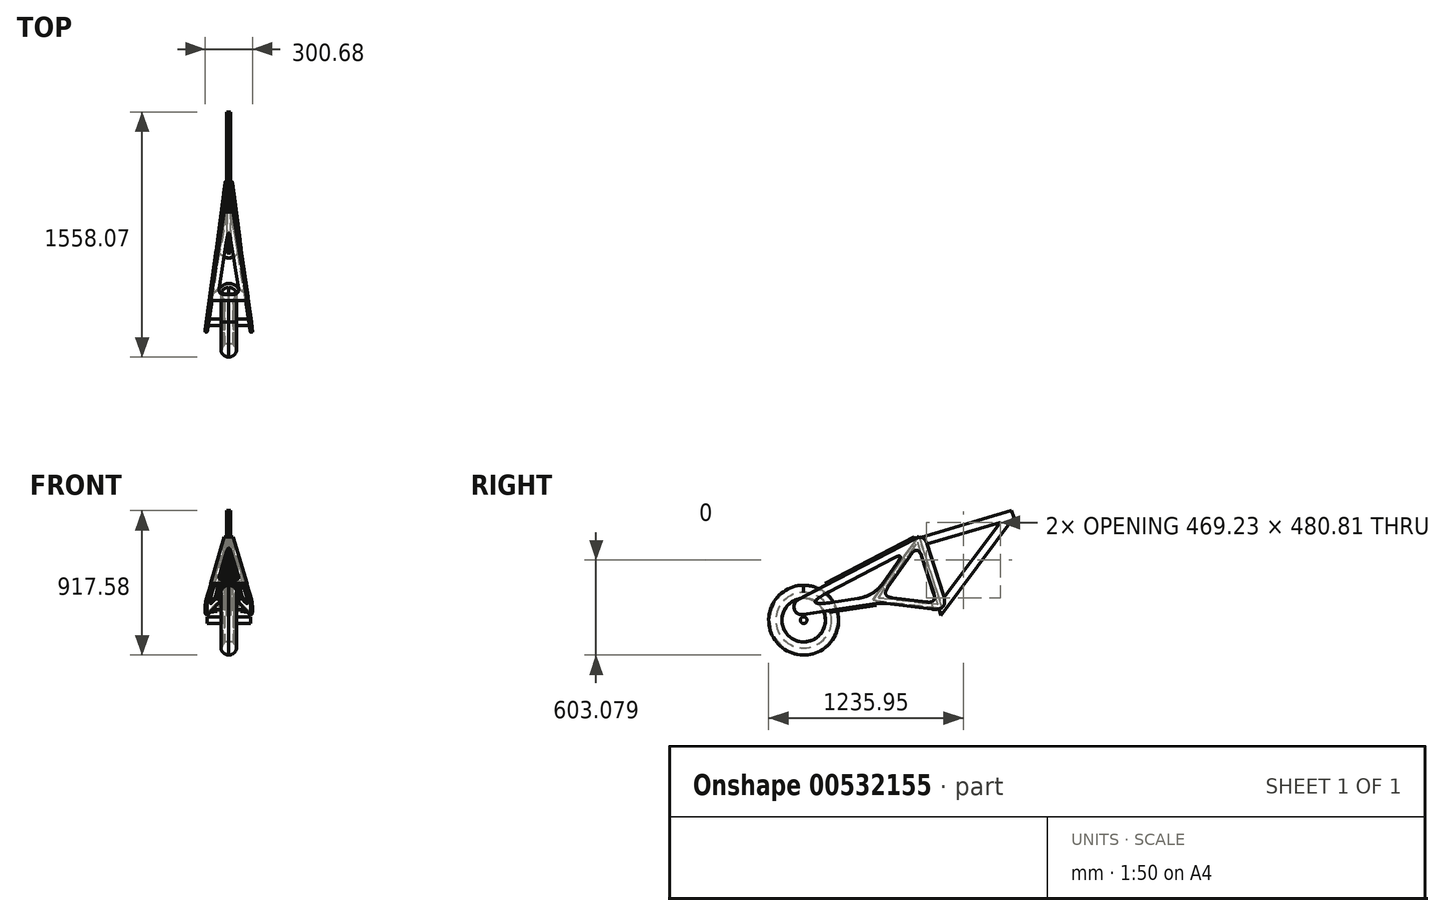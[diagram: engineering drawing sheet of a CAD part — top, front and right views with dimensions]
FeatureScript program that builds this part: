
annotation { "Feature Type Name" : "Feature", "Feature Type Description" : "" }
export const myFeature = defineFeature(function(context is Context, id is Id, definition is map)
    precondition{}
    {
        {
            var Q0;
            Q0=qCreatedBy(makeId("Right.planeOp"),FACE);
            var sketch = newSketch(context, id + "F0", { "sketchPlane" : qUnion([Q0])});
            skLineSegment(sketch, "E0", {"start": v(-1122.6, -29.4) * mm, "end": v(-831.27, 379.28) * mm});
            skLineSegment(sketch, "E1", {"start": v(-831.27, 379.28) * mm, "end": v(-682.15, -80.49) * mm});
            skLineSegment(sketch, "E2", {"start": v(-682.15, -80.49) * mm, "end": v(-235.77, 518.94) * mm});
            skLineSegment(sketch, "E3", {"start": v(-820.77, 346.9) * mm, "end": v(-235.77, 518.94) * mm});
            skLineSegment(sketch, "E4", {"start": v(-1122.6, -29.4) * mm, "end": v(-682.15, -80.49) * mm});
            skLineSegment(sketch, "E5", {"start": v(-291.82, 608.35) * mm, "end": v(115.38, -439.2) * mm});
            skLineSegment(sketch, "E6", {"start": v(-14.33, -30.36) * mm, "end": v(-39.71, -40.22) * mm});
            skLineSegment(sketch, "E7", {"start": v(-14.33, -30.36) * mm, "end": v(-14.33, -432.63) * mm});
            skLineSegment(sketch, "E8", {"start": v(-14.33, -30.36) * mm, "end": v(149.04, -450.65) * mm});
            skSolve(sketch);
        }
        {
            var Q0;
            Q0=qCreatedBy(makeId("Right.planeOp"),FACE);
            var sketch = newSketch(context, id + "F1", { "sketchPlane" : qUnion([Q0])});
            skCircle(sketch, "E9", {"center": v(-1562.05, -156.67) * mm, "radius": 222 * mm});
            skLineSegment(sketch, "E10", {"start": v(660.86, -378.67) * mm, "end": v(-1840.95, -378.67) * mm, "construction": true});
            skSolve(sketch);
        }
        {
            var Q0;
            Q0=qCreatedBy(makeId("Front.planeOp"),FACE);
            var sketch = newSketch(context, id + "F2", { "sketchPlane" : qUnion([Q0])});
            skLineSegment(sketch, "E11.0", {"start": v(0, 65.33) * mm, "end": v(0, -378.67) * mm, "construction": true});
            skFitSpline(sketch, "E12", {"points": [v(0, 65.33) * mm, v(-50, 19.93) * mm], "startDerivative": vector(-52.78, 0) * mm, "endDerivative": vector(0, -87.78) * mm});
            skFitSpline(sketch, "E13", {"points": [v(-50, 19.93) * mm, v(-31.08, -18.17) * mm], "startDerivative": vector(0, -29.8) * mm, "endDerivative": vector(32.97, -29.47) * mm});
            skFitSpline(sketch, "E14.0", {"points": [v(-44.5, 19.93) * mm, v(-44.5, 19.5) * mm, v(-44.46, 18.5) * mm, v(-44.16, 16.18) * mm, v(-43.4, 12.74) * mm, v(-41.86, 8.1) * mm, v(-39.08, 1.57) * mm, v(-35.33, -4.96) * mm, v(-30.93, -10.62) * mm, v(-28.6, -13.01) * mm, v(-27.42, -14.07) * mm]});
            skFitSpline(sketch, "E14.1", {"points": [v(0, 59.83) * mm, v(-0.89, 59.83) * mm, v(-2.83, 59.73) * mm, v(-7.2, 59.08) * mm, v(-13.33, 57.4) * mm, v(-21.02, 54.03) * mm, v(-28.45, 49.4) * mm, v(-35.02, 43.58) * mm, v(-40.22, 36.74) * mm, v(-43.64, 28.95) * mm, v(-44.5, 23.08) * mm, v(-44.5, 19.93) * mm]});
            skLineSegment(sketch, "E15", {"start": v(0, 65.33) * mm, "end": v(0, 59.83) * mm});
            skLineSegment(sketch, "E16", {"start": v(-31.08, -18.17) * mm, "end": v(-27.42, -14.07) * mm});
            skPoint(sketch, "E17", {"position": v(0, -156.67) * mm});
            skSolve(sketch);
        }
        {
            var Q0;
            Q0=qCreatedBy(makeId("Right.planeOp"),FACE);
            var sketch = newSketch(context, id + "F3", { "sketchPlane" : qUnion([Q0])});
            skLineSegment(sketch, "E18.0", {"start": v(0, 65.33) * mm, "end": v(0, -378.67) * mm, "construction": true});
            skPoint(sketch, "E18.1", {"position": v(0, -156.67) * mm});
            skCircle(sketch, "E19", {"center": v(0, -156.67) * mm, "radius": 222 * mm});
            skSolve(sketch);
        }
        {
            var Q0;
            Q0 = qSketchRegion(id + "F2", true);
            var Q1;
            Q1=sQuery(id+"F3.wireOp",EDGE,"E19");
            revolve(context, id + "F4", {"entities" : qUnion([Q0]), "axis" : qUnion([Q1]), "revolveType" : RevolveType.FULL});
        }
        {
            var Q0;
            Q0=makeQuery(id+"F4.opRevolve","SWEPT_BODY",BODY,{"disambiguationData":[OSD([sQuery(id+"F2.wireOp",EDGE,"E12"),sQuery(id+"F2.wireOp",EDGE,"E13"),sQuery(id+"F2.wireOp",EDGE,"E14.0"),sQuery(id+"F2.wireOp",EDGE,"E14.1"),sQuery(id+"F2.wireOp",EDGE,"E15"),sQuery(id+"F2.wireOp",EDGE,"E16")])]});
            var Q1;
            Q1=qCreatedBy(makeId("Right.planeOp"),FACE);
            mirror(context, id + "F5", {"operationType" : NewBodyOperationType.ADD, "entities" : qUnion([Q0]), "mirrorPlane" : qUnion([Q1])});
        }
        {
            var Q0;
            Q0=sQuery(id+"F2.wireOp",EDGE,"E11.0");
            cPoint(context, id + "F6", {"entities" : qUnion([Q0]), "parameter" : 0.5});
        }
        {
            var Q0;
            Q0=makeQuery(id+"F4.opRevolve","SWEPT_BODY",BODY,{"disambiguationData":[OSD([sQuery(id+"F2.wireOp",EDGE,"E12"),sQuery(id+"F2.wireOp",EDGE,"E13"),sQuery(id+"F2.wireOp",EDGE,"E14.0"),sQuery(id+"F2.wireOp",EDGE,"E14.1"),sQuery(id+"F2.wireOp",EDGE,"E15"),sQuery(id+"F2.wireOp",EDGE,"E16")])]});
            var Q1;
            Q1 = qCreatedBy(id + "F6" ,VERTEX);
            var Q2;
            Q2=sQuery(id+"F1.wireOp",VERTEX,"E9.center");
            transform(context, id + "F7", {"entities" : qUnion([Q0]), "transformType" : TransformType.TRANSLATION_ENTITY, "oppositeDirectionEntity" : false, "transformLine" : qUnion([Q1, Q2]), "makeCopy" : false});
        }
        {
            var Q0;
            Q0=qCreatedBy(makeId("Right.planeOp"),FACE);
            var sketch = newSketch(context, id + "F8", { "sketchPlane" : qUnion([Q0])});
            skCircle(sketch, "E20.0.0", {"center": v(-1562.05, -156.67) * mm, "radius": 222 * mm, "construction": true});
            skCircle(sketch, "E21", {"center": v(-1562.05, -156.67) * mm, "radius": 21.1 * mm});
            skSolve(sketch);
        }
        {
            var Q0;
            Q0 = qSketchRegion(id + "F8", true);
            extrude(context, id + "F9", {"entities" : qUnion([Q0]), "endBound" : BoundingType.SYMMETRIC, "depth" : 275 * mm, "offsetDistance" : 25 * mm});
        }
        {
            var Q0;
            Q0=qCreatedBy(makeId("Right.planeOp"),FACE);
            var sketch = newSketch(context, id + "F10", { "sketchPlane" : qUnion([Q0])});
            skCircle(sketch, "E22.0.0", {"center": v(-1562.05, -156.67) * mm, "radius": 222 * mm, "construction": true});
            skCircle(sketch, "E23", {"center": v(-1562.05, -156.67) * mm, "radius": 137.5 * mm});
            skSolve(sketch);
        }
        {
            var Q0;
            Q0 = qSketchRegion(id + "F10", true);
            extrude(context, id + "F11", {"entities" : qUnion([Q0]), "operationType" : NewBodyOperationType.ADD, "endBound" : BoundingType.SYMMETRIC, "depth" : 70 * mm, "offsetDistance" : 25 * mm});
        }
        {
            var Q0;
            {var subQ0=sQuery(id+"F0.wireOp",EDGE,"E0");Q0=makeQuery(id+"F0.imprint","IMPRINT",FACE,{"disambiguationData":[TD([[makeQuery(id+"F0.imprint","IMPRINT",EDGE,{"derivedFrom":subQ0}),-1.0]])]});}
            extrude(context, id + "F12", {"entities" : qUnion([Q0]), "depth" : (135 / 2) * mm, "offsetDistance" : 25 * mm});
        }
        {
            var Q0;
            Q0=makeQuery(id+"F12.opExtrude","CAP_EDGE",EDGE,{"disambiguationData":[OSD([sQuery(id+"F0.wireOp",EDGE,"E1")])],"isStart":false});
            chamfer(context, id + "F13", {"entities" : qUnion([Q0]), "chamferType" : ChamferType.OFFSET_ANGLE, "width" : 55 * mm, "oppositeDirection" : false, "angle" : 82 * degree, "tangentPropagation" : true});
        }
        {
            var Q0;
            Q0=makeQuery(id+"F12.opExtrude","SWEPT_BODY",BODY,{"disambiguationData":[OSD([sQuery(id+"F0.wireOp",EDGE,"E0"),sQuery(id+"F0.wireOp",EDGE,"E1"),sQuery(id+"F0.wireOp",EDGE,"E4")])]});
            var Q1;
            Q1=qCreatedBy(makeId("Right.planeOp"),FACE);
            mirror(context, id + "F14", {"operationType" : NewBodyOperationType.ADD, "entities" : qUnion([Q0]), "mirrorPlane" : qUnion([Q1])});
        }
        {
            var Q0;
            {var subQ0=makeQuery(id+"F12.opExtrude","SWEPT_FACE",FACE,{"disambiguationData":[OSD([sQuery(id+"F0.wireOp",EDGE,"E0")])]});Q0=makeQuery(id+"F14.boolean.opBoolean","MERGE",FACE,{"derivedFrom":[subQ0,makeQuery(id+"F14.opPattern","COPY",FACE,{"derivedFrom":subQ0,"instanceName":"1"})]});}
            var Q1;
            {var subQ0=makeQuery(id+"F12.opExtrude","SWEPT_FACE",FACE,{"disambiguationData":[OSD([sQuery(id+"F0.wireOp",EDGE,"E4")])]});Q1=makeQuery(id+"F14.boolean.opBoolean","MERGE",FACE,{"derivedFrom":[subQ0,makeQuery(id+"F14.opPattern","COPY",FACE,{"derivedFrom":subQ0,"instanceName":"1"})]});}
            shell(context, id + "F15", {"entities" : qUnion([Q0, Q1]), "thickness" : 10 * mm});
        }
        {
            var Q0;
            Q0=qCreatedBy(makeId("Right.planeOp"),FACE);
            var sketch = newSketch(context, id + "F16", { "sketchPlane" : qUnion([Q0])});
            skLineSegment(sketch, "E24.0.0", {"start": v(-1114.03, -17.39) * mm, "end": v(-831.27, 379.28) * mm, "construction": true});
            skLineSegment(sketch, "E24.0.1", {"start": v(-1114.03, -17.39) * mm, "end": v(-1109.65, -30.9) * mm, "construction": true});
            skLineSegment(sketch, "E24.0.2", {"start": v(-682.15, -80.49) * mm, "end": v(-1109.65, -30.9) * mm, "construction": true});
            skLineSegment(sketch, "E24.0.3", {"start": v(-682.15, -80.49) * mm, "end": v(-831.27, 379.28) * mm, "construction": true});
            skLineSegment(sketch, "E25.0", {"start": v(-709.35, -58.2) * mm, "end": v(-837.7, 337.53) * mm});
            skLineSegment(sketch, "E25.1", {"start": v(-709.35, -58.2) * mm, "end": v(-1088.45, -14.23) * mm});
            skLineSegment(sketch, "E25.2", {"start": v(-1088.45, -14.23) * mm, "end": v(-837.7, 337.53) * mm});
            skSolve(sketch);
        }
        {
            var Q0;
            Q0 = qSketchRegion(id + "F16", true);
            var Q1;
            Q1 = qConstructionFilter(qBodyType(qCreatedBy(id + "F16" ,EDGE), BodyType.WIRE), ConstructionObject.NO);
            extrude(context, id + "F17", {"entities" : qUnion([Q0]), "operationType" : NewBodyOperationType.REMOVE, "surfaceEntities" : qUnion([Q1]), "endBound" : BoundingType.SYMMETRIC, "depth" : 174 * mm, "offsetDistance" : 25 * mm});
        }
        {
            var Q0;
            Q0=qCreatedBy(makeId("Right.planeOp"),FACE);
            var sketch = newSketch(context, id + "F18", { "sketchPlane" : qUnion([Q0])});
            skLineSegment(sketch, "E26.0.0", {"start": v(-820.77, 346.9) * mm, "end": v(-682.15, -80.49) * mm, "construction": true});
            skLineSegment(sketch, "E26.0.1", {"start": v(-682.15, -80.49) * mm, "end": v(-249.76, 500.15) * mm, "construction": true});
            skLineSegment(sketch, "E26.0.2", {"start": v(-249.76, 500.15) * mm, "end": v(-254.88, 513.32) * mm, "construction": true});
            skLineSegment(sketch, "E26.0.3", {"start": v(-254.88, 513.32) * mm, "end": v(-820.77, 346.9) * mm, "construction": true});
            skLineSegment(sketch, "E27.0", {"start": v(-242.3, 538.9) * mm, "end": v(-847.4, 360.96) * mm});
            skLineSegment(sketch, "E27.1", {"start": v(-225.98, 496.93) * mm, "end": v(-242.3, 538.9) * mm});
            skLineSegment(sketch, "E27.2", {"start": v(-689.59, -125.63) * mm, "end": v(-225.98, 496.93) * mm});
            skLineSegment(sketch, "E27.3", {"start": v(-847.4, 360.96) * mm, "end": v(-689.59, -125.63) * mm});
            skLineSegment(sketch, "E28.0", {"start": v(-782.71, 326.82) * mm, "end": v(-671.53, -16) * mm});
            skLineSegment(sketch, "E28.1", {"start": v(-313.48, 464.81) * mm, "end": v(-782.71, 326.82) * mm});
            skLineSegment(sketch, "E28.2", {"start": v(-671.53, -16) * mm, "end": v(-313.48, 464.81) * mm});
            skSolve(sketch);
        }
        {
            var Q0;
            Q0 = qSketchRegion(id + "F18", true);
            var Q1;
            {var subQ0=sQuery(id+"F0.wireOp",EDGE,"E1");Q1=makeQuery(id+"F13.opChamfer","BLEND_VERTEX",VERTEX,{"blendedFrom":[makeQuery(id+"F12.opExtrude","CAP_EDGE",EDGE,{"disambiguationData":[OSD([subQ0])],"isStart":false}),makeQuery(id+"F12.opExtrude","SWEPT_FACE",FACE,{"disambiguationData":[OSD([sQuery(id+"F0.wireOp",EDGE,"E0")])]}),makeQuery(id+"F12.opExtrude","SWEPT_FACE",FACE,{"disambiguationData":[OSD([subQ0])]})],"blendedInto":[makeQuery(id+"F12.opExtrude","SWEPT_FACE",FACE,{"disambiguationData":[OSD([sQuery(id+"F0.wireOp",EDGE,"E0")])]}),makeQuery(id+"F12.opExtrude","SWEPT_FACE",FACE,{"disambiguationData":[OSD([subQ0])]})]});}
            extrude(context, id + "F19", {"entities" : qUnion([Q0]), "operationType" : NewBodyOperationType.ADD, "endBound" : BoundingType.UP_TO_VERTEX, "depth" : 25 * mm, "endBoundEntityVertex" : qUnion([Q1]), "offsetDistance" : 25 * mm});
        }
        {
            var Q0;
            Q0=makeQuery(id+"F12.opExtrude","SWEPT_BODY",BODY,{"disambiguationData":[OSD([sQuery(id+"F0.wireOp",EDGE,"E0"),sQuery(id+"F0.wireOp",EDGE,"E1"),sQuery(id+"F0.wireOp",EDGE,"E4")])]});
            var Q1;
            Q1=qCreatedBy(makeId("Right.planeOp"),FACE);
            mirror(context, id + "F20", {"operationType" : NewBodyOperationType.ADD, "entities" : qUnion([Q0]), "mirrorPlane" : qUnion([Q1])});
        }
        {
            var Q0;
            Q0=makeQuery(id+"F13.opChamfer","BLEND_FACE",FACE,{"disambiguationData":[OSD([sQuery(id+"F0.wireOp",EDGE,"E1")])]});
            var sketch = newSketch(context, id + "F21", { "sketchPlane" : qUnion([Q0])});
            skLineSegment(sketch, "E29.0", {"start": v(-711.61, -51.04) * mm, "end": v(-834.34, 323.68) * mm});
            skLineSegment(sketch, "E29.1", {"start": v(-1068, -9.4) * mm, "end": v(-711.61, -51.04) * mm});
            skLineSegment(sketch, "E29.2", {"start": v(-834.34, 323.68) * mm, "end": v(-1068, -9.4) * mm});
            skLineSegment(sketch, "E30.0", {"start": v(-634.82, -108.8) * mm, "end": v(-797.78, 388.75) * mm});
            skLineSegment(sketch, "E31.0", {"start": v(-919.6, 271.8) * mm, "end": v(-1115.15, -6.97) * mm});
            skLineSegment(sketch, "E32", {"start": v(-1634.51, -50.02) * mm, "end": v(-797.78, 388.75) * mm});
            skLineSegment(sketch, "E33.0", {"start": v(-1590.61, -80.07) * mm, "end": v(-919.6, 271.8) * mm});
            skLineSegment(sketch, "E34.0", {"start": v(-1069.42, -49.51) * mm, "end": v(-637.72, -99.95) * mm});
            skLineSegment(sketch, "E35", {"start": v(-1069.42, -49.51) * mm, "end": v(-1618.77, -133.97) * mm});
            skLineSegment(sketch, "E36", {"start": v(-1618.77, -133.97) * mm, "end": v(-1634.51, -50.02) * mm});
            skLineSegment(sketch, "E37.0", {"start": v(-1115.15, -6.97) * mm, "end": v(-1590.61, -80.07) * mm});
            skSolve(sketch);
        }
        {
            var Q0;
            Q0 = qSketchRegion(id + "F21", true);
            extrude(context, id + "F22", {"entities" : qUnion([Q0]), "depth" : 12 * mm, "offsetDistance" : 25 * mm});
        }
        {
            var Q0;
            Q0=makeQuery(id+"F22.opExtrude","SWEPT_EDGE",EDGE,{"disambiguationData":[OSD([sQuery(id+"F21.wireOp",EDGE,"E33.0"),sQuery(id+"F21.wireOp",EDGE,"E37.0")])]});
            fillet(context, id + "F23", {"entities" : qUnion([Q0]), "radius" : 34.8 * mm, "tangentPropagation" : true, "rho" : 0.5, "crossSection" : FilletCrossSection.CONIC, "allowEdgeOverflow" : false});
        }
        {
            var Q0;
            Q0=makeQuery(id+"F22.opExtrude","SWEPT_EDGE",EDGE,{"disambiguationData":[OSD([sQuery(id+"F21.wireOp",EDGE,"E31.0"),sQuery(id+"F21.wireOp",EDGE,"E33.0")])]});
            fillet(context, id + "F24", {"entities" : qUnion([Q0]), "radius" : 18.98 * mm, "tangentPropagation" : true, "rho" : 0.5, "crossSection" : FilletCrossSection.CONIC, "allowEdgeOverflow" : false});
        }
        {
            var Q0;
            Q0=makeQuery(id+"F22.opExtrude","SWEPT_EDGE",EDGE,{"disambiguationData":[OSD([sQuery(id+"F21.wireOp",EDGE,"E31.0"),sQuery(id+"F21.wireOp",EDGE,"E37.0")])]});
            var Q1;
            Q1=makeQuery(id+"F22.opExtrude","SWEPT_EDGE",EDGE,{"disambiguationData":[OSD([sQuery(id+"F21.wireOp",EDGE,"E34.0"),sQuery(id+"F21.wireOp",EDGE,"E35")])]});
            fillet(context, id + "F25", {"entities" : qUnion([Q0, Q1]), "radius" : 253.46 * mm, "tangentPropagation" : true, "rho" : 0.5, "crossSection" : FilletCrossSection.CONIC, "allowEdgeOverflow" : false});
        }
        {
            var Q0;
            Q0=makeQuery(id+"F22.opExtrude","SWEPT_EDGE",EDGE,{"disambiguationData":[OSD([sQuery(id+"F21.wireOp",EDGE,"E29.1"),sQuery(id+"F21.wireOp",EDGE,"E29.2")])]});
            var Q1;
            Q1=makeQuery(id+"F22.opExtrude","SWEPT_EDGE",EDGE,{"disambiguationData":[OSD([sQuery(id+"F21.wireOp",EDGE,"E29.0"),sQuery(id+"F21.wireOp",EDGE,"E29.2")])]});
            var Q2;
            Q2=makeQuery(id+"F22.opExtrude","SWEPT_EDGE",EDGE,{"disambiguationData":[OSD([sQuery(id+"F21.wireOp",EDGE,"E29.0"),sQuery(id+"F21.wireOp",EDGE,"E29.1")])]});
            fillet(context, id + "F26", {"entities" : qUnion([Q0, Q1, Q2]), "radius" : 43.22 * mm, "tangentPropagation" : true, "rho" : 0.5, "crossSection" : FilletCrossSection.CONIC, "allowEdgeOverflow" : false});
        }
        {
            var Q0;
            Q0=makeQuery(id+"F22.opExtrude","SWEPT_EDGE",EDGE,{"disambiguationData":[OSD([sQuery(id+"F21.wireOp",EDGE,"E30.0"),sQuery(id+"F21.wireOp",EDGE,"E34.0")])]});
            fillet(context, id + "F27", {"entities" : qUnion([Q0]), "radius" : 70.1 * mm, "tangentPropagation" : true, "rho" : 0.5, "crossSection" : FilletCrossSection.CONIC, "allowEdgeOverflow" : false});
        }
        {
            var Q0;
            Q0=makeQuery(id+"F22.opExtrude","SWEPT_EDGE",EDGE,{"disambiguationData":[OSD([sQuery(id+"F21.wireOp",EDGE,"E30.0"),sQuery(id+"F21.wireOp",EDGE,"E32")])]});
            fillet(context, id + "F28", {"entities" : qUnion([Q0]), "radius" : 54.23 * mm, "tangentPropagation" : true, "rho" : 0.5, "crossSection" : FilletCrossSection.CONIC, "allowEdgeOverflow" : false});
        }
        {
            var Q0;
            Q0=makeQuery(id+"F22.opExtrude","SWEPT_EDGE",EDGE,{"disambiguationData":[OSD([sQuery(id+"F21.wireOp",EDGE,"E35"),sQuery(id+"F21.wireOp",EDGE,"E36")])]});
            var Q1;
            Q1=makeQuery(id+"F22.opExtrude","SWEPT_EDGE",EDGE,{"disambiguationData":[OSD([sQuery(id+"F21.wireOp",EDGE,"E32"),sQuery(id+"F21.wireOp",EDGE,"E36")])]});
            fillet(context, id + "F29", {"entities" : qUnion([Q0, Q1]), "radius" : 55.18 * mm, "tangentPropagation" : true, "rho" : 0.5, "crossSection" : FilletCrossSection.CONIC, "allowEdgeOverflow" : false});
        }
        {
            var Q0;
            Q0=makeQuery(id+"F22.opExtrude","SWEPT_BODY",BODY,{"disambiguationData":[OSD([sQuery(id+"F21.wireOp",EDGE,"E29.0"),sQuery(id+"F21.wireOp",EDGE,"E29.1"),sQuery(id+"F21.wireOp",EDGE,"E29.2"),sQuery(id+"F21.wireOp",EDGE,"6da51f72-84aa-4f4f-bf31-fd4d25252199.0"),sQuery(id+"F21.wireOp",EDGE,"E30.0"),sQuery(id+"F21.wireOp",EDGE,"E31.0"),sQuery(id+"F21.wireOp",EDGE,"LE8Z4zwS-jpNQ-33Xu-anEL-P9uhT3QDLyb7"),sQuery(id+"F21.wireOp",EDGE,"292b67fa-2026-495d-969f-669d1d39df75.0"),sQuery(id+"F21.wireOp",EDGE,"51c220b2-5f74-4f39-8bed-7295a8b32c18.trimOffspring"),sQuery(id+"F21.wireOp",EDGE,"45e865d4-9d95-4cce-95a6-58d17cf9b12f.0")])]});
            var Q1;
            Q1=qCreatedBy(makeId("Right.planeOp"),FACE);
            mirror(context, id + "F30", {"entities" : qUnion([Q0]), "mirrorPlane" : qUnion([Q1])});
        }
        {
            var Q0;
            {var subQ0=sQuery(id+"F21.wireOp",EDGE,"E36");var subQ1=sQuery(id+"F21.wireOp",EDGE,"E32");Q0=makeQuery(id+"F30.opPattern","COPY",VERTEX,{"derivedFrom":makeQuery(id+"F29.opFillet","BLEND_VERTEX",VERTEX,{"blendedFrom":[makeQuery(id+"F22.opExtrude","SWEPT_EDGE",EDGE,{"disambiguationData":[OSD([subQ1,subQ0])]}),makeQuery(id+"F22.opExtrude","SWEPT_FACE",FACE,{"disambiguationData":[OSD([subQ1])]}),makeQuery(id+"F22.opExtrude","CAP_FACE",FACE,{"disambiguationData":[OSD([sQuery(id+"F21.wireOp",EDGE,"E29.0"),sQuery(id+"F21.wireOp",EDGE,"E29.1"),sQuery(id+"F21.wireOp",EDGE,"E29.2"),sQuery(id+"F21.wireOp",EDGE,"E30.0"),sQuery(id+"F21.wireOp",EDGE,"E31.0"),subQ1,sQuery(id+"F21.wireOp",EDGE,"E33.0"),sQuery(id+"F21.wireOp",EDGE,"E34.0"),sQuery(id+"F21.wireOp",EDGE,"E35"),subQ0,sQuery(id+"F21.wireOp",EDGE,"E37.0")])],"isStart":true})],"blendedInto":[makeQuery(id+"F22.opExtrude","SWEPT_FACE",FACE,{"disambiguationData":[OSD([subQ1])]}),makeQuery(id+"F22.opExtrude","CAP_FACE",FACE,{"disambiguationData":[OSD([sQuery(id+"F21.wireOp",EDGE,"E29.0"),sQuery(id+"F21.wireOp",EDGE,"E29.1"),sQuery(id+"F21.wireOp",EDGE,"E29.2"),sQuery(id+"F21.wireOp",EDGE,"E30.0"),sQuery(id+"F21.wireOp",EDGE,"E31.0"),subQ1,sQuery(id+"F21.wireOp",EDGE,"E33.0"),sQuery(id+"F21.wireOp",EDGE,"E34.0"),sQuery(id+"F21.wireOp",EDGE,"E35"),subQ0,sQuery(id+"F21.wireOp",EDGE,"E37.0")])],"isStart":true})]}),"instanceName":"1"});}
            var Q1;
            {var subQ0=sQuery(id+"F21.wireOp",EDGE,"E36");var subQ1=sQuery(id+"F21.wireOp",EDGE,"E32");Q1=makeQuery(id+"F29.opFillet","BLEND_VERTEX",VERTEX,{"blendedFrom":[makeQuery(id+"F22.opExtrude","SWEPT_EDGE",EDGE,{"disambiguationData":[OSD([subQ1,subQ0])]}),makeQuery(id+"F22.opExtrude","SWEPT_FACE",FACE,{"disambiguationData":[OSD([subQ1])]}),makeQuery(id+"F22.opExtrude","CAP_FACE",FACE,{"disambiguationData":[OSD([sQuery(id+"F21.wireOp",EDGE,"E29.0"),sQuery(id+"F21.wireOp",EDGE,"E29.1"),sQuery(id+"F21.wireOp",EDGE,"E29.2"),sQuery(id+"F21.wireOp",EDGE,"E30.0"),sQuery(id+"F21.wireOp",EDGE,"E31.0"),subQ1,sQuery(id+"F21.wireOp",EDGE,"E33.0"),sQuery(id+"F21.wireOp",EDGE,"E34.0"),sQuery(id+"F21.wireOp",EDGE,"E35"),subQ0,sQuery(id+"F21.wireOp",EDGE,"E37.0")])],"isStart":true})],"blendedInto":[makeQuery(id+"F22.opExtrude","SWEPT_FACE",FACE,{"disambiguationData":[OSD([subQ1])]}),makeQuery(id+"F22.opExtrude","CAP_FACE",FACE,{"disambiguationData":[OSD([sQuery(id+"F21.wireOp",EDGE,"E29.0"),sQuery(id+"F21.wireOp",EDGE,"E29.1"),sQuery(id+"F21.wireOp",EDGE,"E29.2"),sQuery(id+"F21.wireOp",EDGE,"E30.0"),sQuery(id+"F21.wireOp",EDGE,"E31.0"),subQ1,sQuery(id+"F21.wireOp",EDGE,"E33.0"),sQuery(id+"F21.wireOp",EDGE,"E34.0"),sQuery(id+"F21.wireOp",EDGE,"E35"),subQ0,sQuery(id+"F21.wireOp",EDGE,"E37.0")])],"isStart":true})]});}
            var Q2;
            {var subQ0=sQuery(id+"F21.wireOp",EDGE,"E32");var subQ1=sQuery(id+"F21.wireOp",EDGE,"E30.0");Q2=makeQuery(id+"F30.opPattern","COPY",VERTEX,{"derivedFrom":makeQuery(id+"F28.opFillet","BLEND_VERTEX",VERTEX,{"blendedFrom":[makeQuery(id+"F22.opExtrude","SWEPT_EDGE",EDGE,{"disambiguationData":[OSD([subQ1,subQ0])]}),makeQuery(id+"F22.opExtrude","SWEPT_FACE",FACE,{"disambiguationData":[OSD([subQ0])]}),makeQuery(id+"F22.opExtrude","CAP_FACE",FACE,{"disambiguationData":[OSD([sQuery(id+"F21.wireOp",EDGE,"E29.0"),sQuery(id+"F21.wireOp",EDGE,"E29.1"),sQuery(id+"F21.wireOp",EDGE,"E29.2"),subQ1,sQuery(id+"F21.wireOp",EDGE,"E31.0"),subQ0,sQuery(id+"F21.wireOp",EDGE,"E33.0"),sQuery(id+"F21.wireOp",EDGE,"E34.0"),sQuery(id+"F21.wireOp",EDGE,"E35"),sQuery(id+"F21.wireOp",EDGE,"E36"),sQuery(id+"F21.wireOp",EDGE,"E37.0")])],"isStart":true})],"blendedInto":[makeQuery(id+"F22.opExtrude","SWEPT_FACE",FACE,{"disambiguationData":[OSD([subQ0])]}),makeQuery(id+"F22.opExtrude","CAP_FACE",FACE,{"disambiguationData":[OSD([sQuery(id+"F21.wireOp",EDGE,"E29.0"),sQuery(id+"F21.wireOp",EDGE,"E29.1"),sQuery(id+"F21.wireOp",EDGE,"E29.2"),subQ1,sQuery(id+"F21.wireOp",EDGE,"E31.0"),subQ0,sQuery(id+"F21.wireOp",EDGE,"E33.0"),sQuery(id+"F21.wireOp",EDGE,"E34.0"),sQuery(id+"F21.wireOp",EDGE,"E35"),sQuery(id+"F21.wireOp",EDGE,"E36"),sQuery(id+"F21.wireOp",EDGE,"E37.0")])],"isStart":true})]}),"instanceName":"1"});}
            cPlane(context, id + "F31", {"entities" : qUnion([Q0, Q1, Q2]), "cplaneType" : CPlaneType.THREE_POINT, "offset" : 25 * mm, "width" : 150 * mm, "height" : 150 * mm});
        }
        {
            var Q0;
            Q0=qCreatedBy(id+"F31.planeOp",FACE);
            var sketch = newSketch(context, id + "F32", { "sketchPlane" : qUnion([Q0])});
            skLineSegment(sketch, "E38.0", {"start": v(-116.88, 1227.68) * mm, "end": v(-28.76, 591.74) * mm});
            skLineSegment(sketch, "E38.1", {"start": v(116.88, 1227.68) * mm, "end": v(28.76, 591.74) * mm});
            skLineSegment(sketch, "E39", {"start": v(-28.76, 591.74) * mm, "end": v(28.76, 591.74) * mm});
            skLineSegment(sketch, "E40", {"start": v(-116.88, 1227.68) * mm, "end": v(116.88, 1227.68) * mm});
            skPoint(sketch, "E41.orphan", {"position": v(-144.04, 1423.7) * mm});
            skPoint(sketch, "E42.orphan", {"position": v(144.04, 1423.7) * mm});
            skLineSegment(sketch, "E43.0", {"start": v(-67.51, 1184.68) * mm, "end": v(0, 697.45) * mm});
            skLineSegment(sketch, "E43.1", {"start": v(-67.51, 1184.68) * mm, "end": v(67.51, 1184.68) * mm});
            skLineSegment(sketch, "E43.2", {"start": v(67.51, 1184.68) * mm, "end": v(0, 697.45) * mm});
            skSolve(sketch);
        }
        {
            var Q0;
            Q0=makeQuery(id+"F32.imprint","IMPRINT",FACE,{"disambiguationData":[TD([[makeQuery(id+"F32.imprint","IMPRINT",EDGE,{"derivedFrom":sQuery(id+"F32.wireOp",EDGE,"E38.0")}),1.0]])]});
            extrude(context, id + "F33", {"entities" : qUnion([Q0]), "oppositeDirection" : true, "depth" : 12 * mm, "offsetDistance" : 25 * mm});
        }
        {
            var Q0;
            Q0=makeQuery(id+"F33.opExtrude","SWEPT_EDGE",EDGE,{"disambiguationData":[OSD([sQuery(id+"F32.wireOp",EDGE,"E43.0"),sQuery(id+"F32.wireOp",EDGE,"E43.1")])]});
            var Q1;
            Q1=makeQuery(id+"F33.opExtrude","SWEPT_EDGE",EDGE,{"disambiguationData":[OSD([sQuery(id+"F32.wireOp",EDGE,"E43.1"),sQuery(id+"F32.wireOp",EDGE,"E43.2")])]});
            fillet(context, id + "F34", {"entities" : qUnion([Q0, Q1]), "radius" : 40.19 * mm, "tangentPropagation" : true, "rho" : 0.5, "crossSection" : FilletCrossSection.CONIC, "allowEdgeOverflow" : false});
        }
        {
            var Q0;
            Q0=makeQuery(id+"F33.opExtrude","SWEPT_EDGE",EDGE,{"disambiguationData":[OSD([sQuery(id+"F32.wireOp",EDGE,"E43.0"),sQuery(id+"F32.wireOp",EDGE,"E43.2")])]});
            fillet(context, id + "F35", {"entities" : qUnion([Q0]), "radius" : 12.9 * mm, "tangentPropagation" : true, "rho" : 0.5, "crossSection" : FilletCrossSection.CONIC, "allowEdgeOverflow" : false});
        }
        {
            var Q0;
            {var subQ0=sQuery(id+"F21.wireOp",EDGE,"E35");var subQ1=sQuery(id+"F21.wireOp",EDGE,"E34.0");Q0=makeQuery(id+"F25.opFillet","BLEND_VERTEX",VERTEX,{"blendedFrom":[makeQuery(id+"F22.opExtrude","SWEPT_EDGE",EDGE,{"disambiguationData":[OSD([subQ1,subQ0])]}),makeQuery(id+"F22.opExtrude","SWEPT_FACE",FACE,{"disambiguationData":[OSD([subQ0])]}),makeQuery(id+"F22.opExtrude","CAP_FACE",FACE,{"disambiguationData":[OSD([sQuery(id+"F21.wireOp",EDGE,"E29.0"),sQuery(id+"F21.wireOp",EDGE,"E29.1"),sQuery(id+"F21.wireOp",EDGE,"E29.2"),sQuery(id+"F21.wireOp",EDGE,"E30.0"),sQuery(id+"F21.wireOp",EDGE,"E31.0"),sQuery(id+"F21.wireOp",EDGE,"E32"),sQuery(id+"F21.wireOp",EDGE,"E33.0"),subQ1,subQ0,sQuery(id+"F21.wireOp",EDGE,"E36"),sQuery(id+"F21.wireOp",EDGE,"E37.0")])],"isStart":true})],"blendedInto":[makeQuery(id+"F22.opExtrude","SWEPT_FACE",FACE,{"disambiguationData":[OSD([subQ0])]}),makeQuery(id+"F22.opExtrude","CAP_FACE",FACE,{"disambiguationData":[OSD([sQuery(id+"F21.wireOp",EDGE,"E29.0"),sQuery(id+"F21.wireOp",EDGE,"E29.1"),sQuery(id+"F21.wireOp",EDGE,"E29.2"),sQuery(id+"F21.wireOp",EDGE,"E30.0"),sQuery(id+"F21.wireOp",EDGE,"E31.0"),sQuery(id+"F21.wireOp",EDGE,"E32"),sQuery(id+"F21.wireOp",EDGE,"E33.0"),subQ1,subQ0,sQuery(id+"F21.wireOp",EDGE,"E36"),sQuery(id+"F21.wireOp",EDGE,"E37.0")])],"isStart":true})]});}
            var Q1;
            {var subQ0=sQuery(id+"F21.wireOp",EDGE,"E35");var subQ1=sQuery(id+"F21.wireOp",EDGE,"E34.0");Q1=makeQuery(id+"F30.opPattern","COPY",VERTEX,{"derivedFrom":makeQuery(id+"F25.opFillet","BLEND_VERTEX",VERTEX,{"blendedFrom":[makeQuery(id+"F22.opExtrude","SWEPT_EDGE",EDGE,{"disambiguationData":[OSD([subQ1,subQ0])]}),makeQuery(id+"F22.opExtrude","SWEPT_FACE",FACE,{"disambiguationData":[OSD([subQ0])]}),makeQuery(id+"F22.opExtrude","CAP_FACE",FACE,{"disambiguationData":[OSD([sQuery(id+"F21.wireOp",EDGE,"E29.0"),sQuery(id+"F21.wireOp",EDGE,"E29.1"),sQuery(id+"F21.wireOp",EDGE,"E29.2"),sQuery(id+"F21.wireOp",EDGE,"E30.0"),sQuery(id+"F21.wireOp",EDGE,"E31.0"),sQuery(id+"F21.wireOp",EDGE,"E32"),sQuery(id+"F21.wireOp",EDGE,"E33.0"),subQ1,subQ0,sQuery(id+"F21.wireOp",EDGE,"E36"),sQuery(id+"F21.wireOp",EDGE,"E37.0")])],"isStart":true})],"blendedInto":[makeQuery(id+"F22.opExtrude","SWEPT_FACE",FACE,{"disambiguationData":[OSD([subQ0])]}),makeQuery(id+"F22.opExtrude","CAP_FACE",FACE,{"disambiguationData":[OSD([sQuery(id+"F21.wireOp",EDGE,"E29.0"),sQuery(id+"F21.wireOp",EDGE,"E29.1"),sQuery(id+"F21.wireOp",EDGE,"E29.2"),sQuery(id+"F21.wireOp",EDGE,"E30.0"),sQuery(id+"F21.wireOp",EDGE,"E31.0"),sQuery(id+"F21.wireOp",EDGE,"E32"),sQuery(id+"F21.wireOp",EDGE,"E33.0"),subQ1,subQ0,sQuery(id+"F21.wireOp",EDGE,"E36"),sQuery(id+"F21.wireOp",EDGE,"E37.0")])],"isStart":true})]}),"instanceName":"1"});}
            var Q2;
            {var subQ0=sQuery(id+"F21.wireOp",EDGE,"E36");var subQ1=sQuery(id+"F21.wireOp",EDGE,"E35");Q2=makeQuery(id+"F30.opPattern","COPY",VERTEX,{"derivedFrom":makeQuery(id+"F29.opFillet","BLEND_VERTEX",VERTEX,{"blendedFrom":[makeQuery(id+"F22.opExtrude","SWEPT_EDGE",EDGE,{"disambiguationData":[OSD([subQ1,subQ0])]}),makeQuery(id+"F22.opExtrude","SWEPT_FACE",FACE,{"disambiguationData":[OSD([subQ1])]}),makeQuery(id+"F22.opExtrude","CAP_FACE",FACE,{"disambiguationData":[OSD([sQuery(id+"F21.wireOp",EDGE,"E29.0"),sQuery(id+"F21.wireOp",EDGE,"E29.1"),sQuery(id+"F21.wireOp",EDGE,"E29.2"),sQuery(id+"F21.wireOp",EDGE,"E30.0"),sQuery(id+"F21.wireOp",EDGE,"E31.0"),sQuery(id+"F21.wireOp",EDGE,"E32"),sQuery(id+"F21.wireOp",EDGE,"E33.0"),sQuery(id+"F21.wireOp",EDGE,"E34.0"),subQ1,subQ0,sQuery(id+"F21.wireOp",EDGE,"E37.0")])],"isStart":true})],"blendedInto":[makeQuery(id+"F22.opExtrude","SWEPT_FACE",FACE,{"disambiguationData":[OSD([subQ1])]}),makeQuery(id+"F22.opExtrude","CAP_FACE",FACE,{"disambiguationData":[OSD([sQuery(id+"F21.wireOp",EDGE,"E29.0"),sQuery(id+"F21.wireOp",EDGE,"E29.1"),sQuery(id+"F21.wireOp",EDGE,"E29.2"),sQuery(id+"F21.wireOp",EDGE,"E30.0"),sQuery(id+"F21.wireOp",EDGE,"E31.0"),sQuery(id+"F21.wireOp",EDGE,"E32"),sQuery(id+"F21.wireOp",EDGE,"E33.0"),sQuery(id+"F21.wireOp",EDGE,"E34.0"),subQ1,subQ0,sQuery(id+"F21.wireOp",EDGE,"E37.0")])],"isStart":true})]}),"instanceName":"1"});}
            cPlane(context, id + "F36", {"entities" : qUnion([Q0, Q1, Q2]), "cplaneType" : CPlaneType.THREE_POINT, "offset" : 25 * mm, "width" : 150 * mm, "height" : 150 * mm});
        }
        {
            var Q0;
            Q0=qCreatedBy(id+"F36.planeOp",FACE);
            var sketch = newSketch(context, id + "F37", { "sketchPlane" : qUnion([Q0])});
            skLineSegment(sketch, "E44.0", {"start": v(-79.58, 1098.28) * mm, "end": v(-121.26, 1398.91) * mm});
            skLineSegment(sketch, "E44.1", {"start": v(79.58, 1098.28) * mm, "end": v(121.26, 1398.91) * mm});
            skLineSegment(sketch, "E45", {"start": v(121.26, 1398.91) * mm, "end": v(0, 1285.53) * mm});
            skLineSegment(sketch, "E46", {"start": v(0, 1285.53) * mm, "end": v(0, 1190.1) * mm, "construction": true});
            skLineSegment(sketch, "E47.MirrorCS", {"start": v(-121.26, 1398.91) * mm, "end": v(0, 1285.53) * mm});
            skPoint(sketch, "E48.orphan", {"position": v(143.86, 1561.98) * mm});
            skPoint(sketch, "E49.orphan", {"position": v(-143.86, 1561.98) * mm});
            skLineSegment(sketch, "E50", {"start": v(79.58, 1098.28) * mm, "end": v(0, 1190.1) * mm});
            skLineSegment(sketch, "E51.MirrorCS", {"start": v(-79.58, 1098.28) * mm, "end": v(0, 1190.1) * mm});
            skSolve(sketch);
        }
        {
            var Q0;
            Q0=makeQuery(id+"F37.imprint","IMPRINT",FACE,{"disambiguationData":[TD([[makeQuery(id+"F37.imprint","IMPRINT",EDGE,{"derivedFrom":sQuery(id+"F37.wireOp",EDGE,"E44.0")}),-1.0]])]});
            extrude(context, id + "F38", {"entities" : qUnion([Q0]), "depth" : 12 * mm, "offsetDistance" : 25 * mm});
        }
        {
            var Q0;
            Q0=makeQuery(id+"F38.opExtrude","SWEPT_EDGE",EDGE,{"disambiguationData":[OSD([sQuery(id+"F37.wireOp",EDGE,"E45"),sQuery(id+"F37.wireOp",EDGE,"E47.MirrorCS")])]});
            fillet(context, id + "F39", {"entities" : qUnion([Q0]), "radius" : 110.28 * mm, "tangentPropagation" : true, "rho" : 0.6, "crossSection" : FilletCrossSection.CONIC, "allowEdgeOverflow" : false});
        }
        {
            var Q0;
            Q0=makeQuery(id+"F38.opExtrude","SWEPT_EDGE",EDGE,{"disambiguationData":[OSD([sQuery(id+"F37.wireOp",EDGE,"E50"),sQuery(id+"F37.wireOp",EDGE,"E51.MirrorCS")])]});
            fillet(context, id + "F40", {"entities" : qUnion([Q0]), "radius" : 89.2 * mm, "tangentPropagation" : true, "rho" : 0.5, "crossSection" : FilletCrossSection.CONIC, "allowEdgeOverflow" : false});
        }
    });
